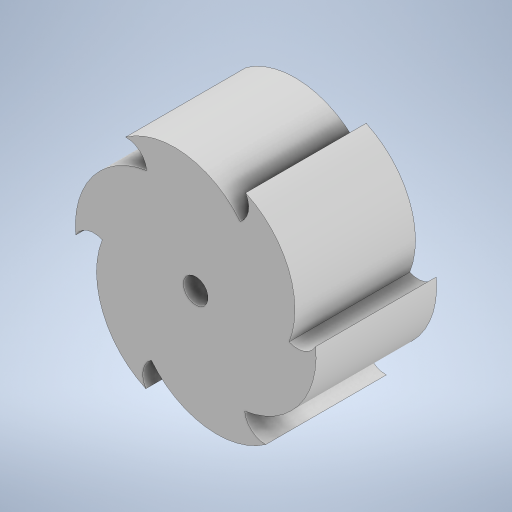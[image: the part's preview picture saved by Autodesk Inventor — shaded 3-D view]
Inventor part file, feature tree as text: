
AUTODESK INVENTOR PART (.ipt)
format: ipt  version: 2023 (Build 270158000, 158)  size: 254,976 bytes
history: native  units: in
note: dims shown in document units (in); Inventor stores cm internally (conversion verified against a paired STEP export)
features: extrude x2, sketch x1
ambient origin geometry x8: Origin, YZ Plane, XZ Plane, XY Plane, X Axis, Y Axis, Z Axis, Center Point
bodies: Solid1 (feature_tree)
feature tree (3):
  sketch  "Sketch1"  dims[d0=2.0in d1=1.5in d3=0.17in d4=0.275in d5=0.125in d6=0.82in d7=2.3622in d9=360.0deg d11=0.205in d12=1.0in d13=0.0in d14=0.0in d15=0.0in]
  extrude  "Extrusion1"  Depth=1.0in
  extrude  "Extrusion2"  Depth=0.17in
